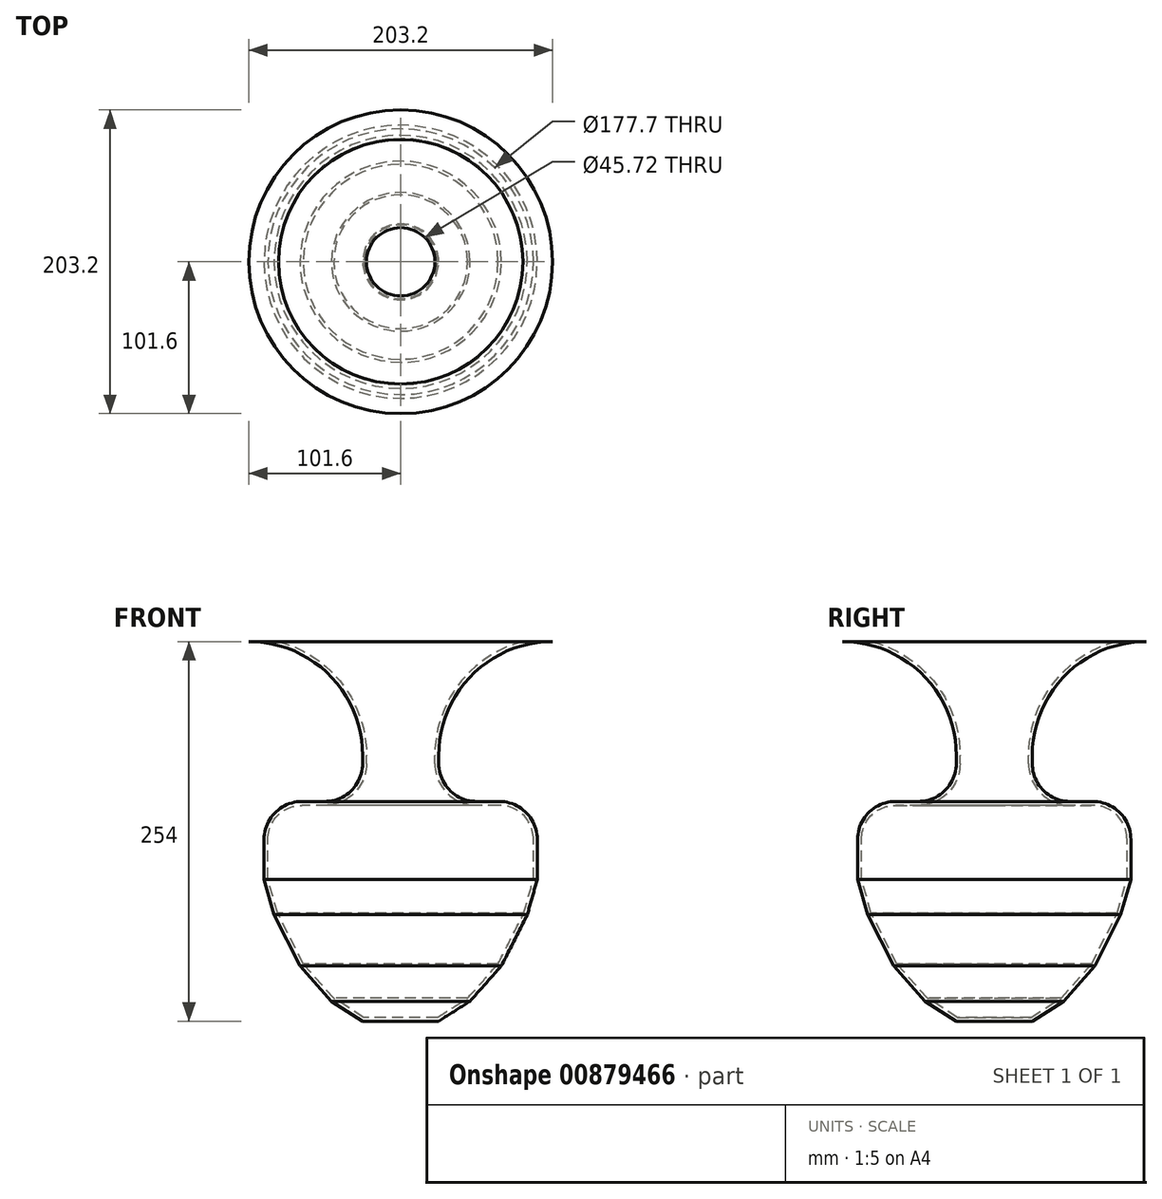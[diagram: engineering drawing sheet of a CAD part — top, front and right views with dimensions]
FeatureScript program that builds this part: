
annotation { "Feature Type Name" : "Feature", "Feature Type Description" : "" }
export const myFeature = defineFeature(function(context is Context, id is Id, definition is map)
    precondition{}
    {
        {
            var Q0;
            Q0=qCreatedBy(makeId("Front.planeOp"),FACE);
            var sketch = newSketch(context, id + "F0", { "sketchPlane" : qUnion([Q0])});
            skLineSegment(sketch, "E0", {"start": v(-25.4, 0) * mm, "end": v(25.4, 0) * mm});
            skLineSegment(sketch, "E1", {"start": v(0, 0) * mm, "end": v(0, 254) * mm, "construction": true});
            skLineSegment(sketch, "E2", {"start": v(-76.2, 254) * mm, "end": v(-101.6, 254) * mm});
            skLineSegment(sketch, "E3", {"start": v(-25.4, 177.8) * mm, "end": v(-25.4, 172.42) * mm});
            skPoint(sketch, "E4.newPointA", {"position": v(0, 254) * mm});
            skArc(sketch, "E4.filletArc", {"start": v(-25.4, 177.8) * mm, "mid": v(-47.72, 231.68) * mm, "end": v(-101.6, 254) * mm});
            skLineSegment(sketch, "E5", {"start": v(-101.6, 254) * mm, "end": v(0, 254) * mm});
            skPoint(sketch, "E6.visualSharp", {"position": v(-25.4, 147.02) * mm});
            skArc(sketch, "E6.filletArc", {"start": v(-50.8, 147.02) * mm, "mid": v(-32.84, 154.46) * mm, "end": v(-25.4, 172.42) * mm});
            skLineSegment(sketch, "E7", {"start": v(-50.8, 147.02) * mm, "end": v(-66, 147.02) * mm});
            skLineSegment(sketch, "E8", {"start": v(-91.4, 121.62) * mm, "end": v(-91.4, 104.68) * mm});
            skPoint(sketch, "E9.visualSharp", {"position": v(-91.4, 147.02) * mm});
            skArc(sketch, "E9.filletArc", {"start": v(-66, 147.02) * mm, "mid": v(-83.95, 139.58) * mm, "end": v(-91.4, 121.62) * mm});
            skLineSegment(sketch, "E10", {"start": v(-91.4, 104.68) * mm, "end": v(-91.4, 94.87) * mm});
            skLineSegment(sketch, "E11", {"start": v(-91.4, 94.87) * mm, "end": v(-84.7, 71.25) * mm});
            skLineSegment(sketch, "E12", {"start": v(-84.7, 71.25) * mm, "end": v(-67.32, 36.93) * mm});
            skLineSegment(sketch, "E13", {"start": v(-67.32, 36.93) * mm, "end": v(-46.38, 13.35) * mm});
            skLineSegment(sketch, "E14", {"start": v(-46.38, 13.35) * mm, "end": v(-25.4, 0) * mm});
            skLineSegment(sketch, "E15", {"start": v(0, 254) * mm, "end": v(0, 0) * mm});
            skSolve(sketch);
        }
        {
            var Q0;
            Q0 = qSketchRegion(id + "F0", true);
            var Q1;
            Q1=sQuery(id+"F0.wireOp",EDGE,"E15");
            revolve(context, id + "F1", {"surfaceOperationType" : NewSurfaceOperationType.NEW, "entities" : qUnion([Q0]), "axis" : qUnion([Q1]), "revolveType" : RevolveType.FULL});
        }
        {
            var Q0;
            Q0=makeQuery(id+"F1.opRevolve","SWEPT_FACE",FACE,{"disambiguationData":[OSD([sQuery(id+"F0.wireOp",EDGE,"E5")])]});
            shell(context, id + "F2", {"entities" : qUnion([Q0]), "thickness" : 2.54 * mm});
        }
    });
